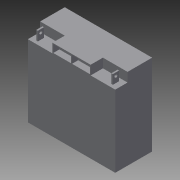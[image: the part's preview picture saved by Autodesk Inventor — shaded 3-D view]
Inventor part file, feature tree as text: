
AUTODESK INVENTOR PART (.ipt)
format: ipt  version: 2015 SP1 (Build 190203100, 203)  size: 208,896 bytes
history: native  units: in
note: dims shown in document units (in); Inventor stores cm internally (conversion verified against a paired STEP export)
features: extrude x7, sketch x7, projected_geometry x7
ambient origin geometry x8: Origin, YZ Plane, XZ Plane, XY Plane, X Axis, Y Axis, Z Axis, Center Point
bodies: Solid1 (feature_tree)
feature tree (21):
  extrude  "Extrusion1"  Depth=3.0in
  extrude  "Extrusion2"  Depth=2.0in
  extrude  "Extrusion3"  Depth=2.0in
  extrude  "Extrusion4"  Depth=0.75in TaperAngle=0.0deg
  extrude  "Extrusion5"  Depth=1.45in
  extrude  "Extrusion6"  Depth=0.5in TaperAngle=0.0deg
  extrude  "Extrusion7"  Depth=1.69in
  sketch  "Sketch1"  dims[d0=7.1in d1=3.0in]
  sketch  "Sketch2"  dims[d2=6.6in d3=0.0in d4=2.0in]
  projected_geometry  "Projected Loop1"
  sketch  "Sketch3"  dims[d5=1.0in d6=2.0in]
  projected_geometry  "Projected Loop2"
  sketch  "Sketch4"  dims[d7=1.0in d8=0.75in d9=0.0in]
  projected_geometry  "Projected Loop3"
  sketch  "Sketch5"  dims[d10=0.0625in d11=1.45in]
  projected_geometry  "Projected Loop4"
  projected_geometry  "Projected Loop5"
  sketch  "Sketch6"  dims[d12=1.45in d13=0.5in d14=0.0in]
  projected_geometry  "Projected Loop6"
  sketch  "Sketch7"  dims[d15=0.0625in d16=1.69in d17=1.69in d18=1.69in d19=1.69in d20=0.0625in d21=0.0625in d22=0.5in d23=0.0in d24=0.5in d25=0.5in d26=0.5in d27=0.5in d28=0.125in d29=0.5in d30=0.125in d31=0.5in d32=0.75in d33=0.0in d34=0.25in d35=0.25in d36=0.25in d37=1.0in d38=0.0in d39=0.25in d40=0.25in d41=0.25in d42=1.0in d43=0.0in]
  projected_geometry  "Projected Loop7"
